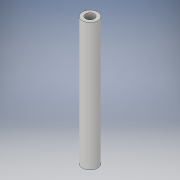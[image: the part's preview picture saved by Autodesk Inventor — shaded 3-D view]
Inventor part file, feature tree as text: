
AUTODESK INVENTOR PART (.ipt)
format: ipt  version: 2019 (Build 230136000, 136)  size: 93,696 bytes
history: native  units: mm
features: extrude x1, sketch x1
ambient origin geometry x8: Origin, YZ Plane, XZ Plane, XY Plane, X Axis, Y Axis, Z Axis, Center Point
bodies: Solid1 (feature_tree)
feature tree (2):
  extrude  "Extrusion1"  Depth=50.0mm
  sketch  "Sketch1"  dims[d0=3.4mm d1=6.0mm d2=50.0mm d3=0.0mm]
